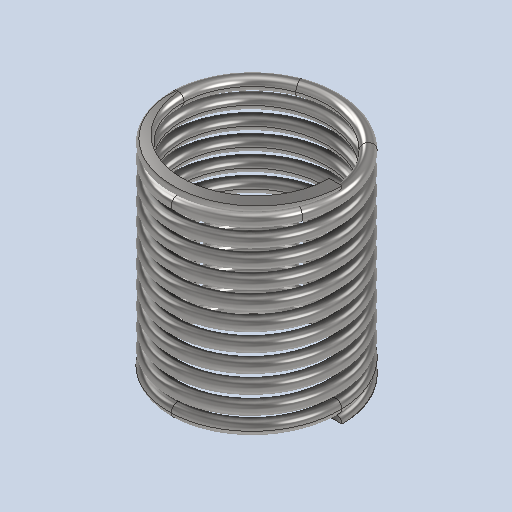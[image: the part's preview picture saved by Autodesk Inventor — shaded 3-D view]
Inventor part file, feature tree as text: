
AUTODESK INVENTOR PART (.ipt)
format: ipt  version: 2025 (Build 290162010, 162A)  size: 1,136,640 bytes
history: native  units: mm
features: other x65, extrude x8, plane x5, helix x3, sketch x3, sweep x2
ambient origin geometry x8: Origin, YZ Plane, XZ Plane, XY Plane, X Axis, Y Axis, Z Axis, Center Point
bodies: Solid1 (feature_tree)
feature tree (86):
  other  "Hauptschraubenpfad(Rechts)"
  other  "Profilarbeitsebene(Rechts)"
  plane  "Arbeitsebene(Rechts) starten"
  plane  "Arbeitsebene(Rechts) beenden"
  other  "Schnittarbeitsebene(Rechts) beenden"
  other  "Schnittarbeitsebene(Rechts) starten"
  other  "Schnittarbeitsebene mit flachen Enden 1(Rechts)"
  other  "Schnittarbeitsebene mit flachen Enden 2(Rechts)"
  sweep  "Main Coil Feature(R)"
  other  "Übergangsschraube 1(Rechts) starten"
  helix  "Coil  Start Transition 2(R)"  [1 undecoded]
  helix  "Coil  Start Transition 3(R)"  [1 undecoded]
  helix  "Coil  Start Transition 4(R)"  [1 undecoded]
  other  "Endenschraube(Rechts) starten"
  extrude  "Schnittelement(Rechts) starten"  Depth=10.0mm
  other  "Übergangsschraube 1(Rechts) beenden"
  other  "Übergangsschraube 2(Rechts) beenden"
  other  "Übergangsschraube 3(Rechts) beenden"
  other  "Übergangsschraube 4(Rechts) beenden"
  other  "Spirale(Rechts) beenden"
  extrude  "Schnittelement(Rechts) beenden"  Depth=10.0mm
  extrude  "Schnittelement mit flachen Enden 1(Rechts)"  Depth=10.0mm
  extrude  "Plain Ends Cut  2(R)"  Depth=10.0mm TaperAngle=0.0deg
  other  "Hauptschraubenpfad(Links)"
  other  "Profilarbeitsebene(Links)"
  plane  "Arbeitsebene(Links) starten"
  plane  "Arbeitsebene(Links) beenden"
  other  "Schnittarbeitsebene(Links) beenden"
  other  "Schnittarbeitsebene(Links) starten"
  other  "Schnittarbeitsebene mit flachen Enden 1(Links)"
  other  "Schnittarbeitsebene mit flachen Enden 2(Links)"
  sweep  "Main Coil Feature(L)"
  other  "Übergangsschraube 1(Links) starten"
  other  "Übergangsschraube 2(Links) starten"
  other  "Übergangsschraube 3(Links) starten"
  other  "Übergangsschraube 4(Links) starten"
  other  "Endenschraube(Links) starten"
  extrude  "Schnittelement(Links) starten"  Depth=10.0mm TaperAngle=0.0deg
  other  "Übergangsschraube 1(Links) beenden"
  other  "Übergangsschraube 2(Links) beenden"
  other  "Übergangsschraube 3(Links) beenden"
  other  "Übergangsschraube 4(Links) beenden"
  other  "Spirale(Links) beenden"
  extrude  "Schnittelement(Links) beenden"  Depth=10.0mm
  extrude  "Cut Plain Ends Cut 1(L)"  TaperAngle=0.0deg  [1 undecoded]
  extrude  "Cut Plain Ends Cut 2(L)"  TaperAngle=0.0deg  [1 undecoded]
  other  "iMate-basierte Arbeitsebene"
  other  "Vorschau Mittelpunkt"
  other  "Vorschau X-Achse"
  other  "Pfadprofilskizze(Rechts)"
  other  "Srf1"
  other  "Spiralenprofilskizze(Rechts)"
  other  "Übergangsschraubenskizze 1(Rechts) starten"
  sketch  "Sketch  Start Transition 2(R)"  dims[d0=0.125mm d2=0.701927mm d3=10.0mm d4=92.5mm]
  sketch  "Sketch  Start Transition 3(R)"  dims[d5=0.0mm d6=90.0deg d7=90.0deg d8=0.0mm d9=0.0mm d12=0.681625mm d13=-0.825556mm d14=0.5mm]
  sketch  "Sketch  Start Transition 4(R)"  dims[d15=0.0mm d16=0.651446mm d17=10.0mm d18=2.5mm d19=0.0mm d20=90.0deg d21=90.0deg d22=0.0mm d23=0.0mm d24=0.600964mm d25=10.0mm d26=2.5mm d27=0.0mm d28=90.0deg d29=90.0deg d30=0.0mm d31=0.0mm d32=0.550482mm d33=10.0mm d34=2.5mm d35=0.0mm d36=90.0deg d37=90.0deg d38=0.0mm d39=0.0mm d40=0.5mm d41=10.0mm d42=2.5mm d43=0.0mm d44=90.0deg d45=90.0deg d46=0.0mm d47=0.0mm d48=0.651446mm d49=10.0mm d50=1.875mm d51=0.0mm d52=90.0deg d53=90.0deg d54=0.0mm d55=0.0mm d56=0.600964mm d57=10.0mm d58=1.875mm d59=0.0mm d60=90.0deg d61=90.0deg d62=0.0mm d63=0.0mm d64=0.550482mm d65=10.0mm d66=1.875mm d67=0.0mm d68=90.0deg d69=90.0deg d70=0.0mm d71=0.0mm d72=0.5mm d73=10.0mm d74=1.875mm d75=0.0mm d76=90.0deg d77=90.0deg d78=0.0mm d79=0.0mm d81=10.0mm d82=5.0mm d83=0.0mm d84=90.0deg d85=90.0deg d86=0.0mm d87=0.0mm d88=0.500334mm d89=10.0mm d90=5.0mm d91=0.0mm d92=90.0deg d93=90.0deg d94=0.0mm d95=0.0mm d96=6.6153mm d97=0.500334mm d98=0.0mm d99=6.6153mm d100=0.500334mm d101=0.0mm d102=0.0mm d103=0.0mm d104=0.0mm d105=0.0mm d106=0.0mm d108=0.0mm d112=0.0mm d113=0.0mm d114=0.0mm d121=0.000334mm d131=0.0mm d132=0.0mm d133=0.0mm d134=0.0mm d135=0.125mm d137=0.701927mm d138=10.0mm d139=92.5mm d140=0.0mm d141=90.0deg d142=90.0deg d143=0.0mm d144=0.0mm d145=0.681625mm d146=-0.825556mm d147=0.000334mm d148=0.000334mm d149=0.5mm d150=0.0mm d151=0.0mm d152=0.651446mm d153=10.0mm d154=2.5mm d155=0.0mm d156=90.0deg d157=90.0deg d158=0.0mm d159=0.0mm d160=0.600964mm d161=10.0mm d162=2.5mm d163=0.0mm d164=90.0deg d165=90.0deg d166=0.0mm d167=0.0mm d168=0.550482mm d169=10.0mm d170=2.5mm d171=0.0mm d172=90.0deg d173=90.0deg d174=0.0mm d175=0.0mm d176=0.5mm d177=10.0mm d178=2.5mm d179=0.0mm d180=90.0deg d181=90.0deg d182=0.0mm d183=0.0mm d184=10.0mm d185=10.0mm d186=10.0mm d187=10.0mm d188=0.500334mm d189=10.0mm d190=5.0mm d191=0.0mm d192=90.0deg d193=90.0deg d194=0.0mm d195=0.0mm d196=10.0mm d197=6.6153mm d198=0.500334mm d199=0.0mm d200=10.0mm d201=0.651446mm d202=10.0mm d203=1.875mm d204=0.0mm d205=90.0deg d206=90.0deg d207=0.0mm d208=0.0mm d209=10.0mm d210=0.600964mm d211=10.0mm d212=1.875mm d213=0.0mm d214=90.0deg d215=90.0deg d216=0.0mm d217=0.0mm d218=0.550482mm d219=10.0mm d220=1.875mm d221=0.0mm d222=90.0deg d223=90.0deg d224=0.0mm d225=0.0mm d226=0.5mm d227=10.0mm d228=1.875mm d229=0.0mm d230=90.0deg d231=90.0deg d232=0.0mm d233=0.0mm d234=10.0mm d235=10.0mm d236=10.0mm d237=0.500334mm d238=10.0mm d239=5.0mm d240=0.0mm d241=90.0deg d242=90.0deg d243=0.0mm d244=0.0mm d245=6.6153mm d246=0.500334mm d247=0.0mm d248=10.0mm d249=10.0mm d254=6.6153mm d255=10.0mm d256=0.0mm d257=20.0mm d258=-0.000334mm d259=6.6153mm d260=10.0mm d261=0.0mm d262=10.0mm d263=6.6153mm d264=10.0mm d265=0.0mm d266=10.0mm d267=0.0mm d270=-0.763056mm d271=0.0mm d272=6.6153mm d273=10.0mm d274=0.0mm d275=20.0mm d276=-94.24778mm d277=6.1153mm d278=6.1153mm d279=0.0mm d280=0.0mm]
  other  "Übergangsschraubenskizze 1(Rechts) beenden"
  other  "Übergangsschraubenskizze 2(Rechts) beenden"
  other  "Übergangsschraubenskizze 3(Rechts) beenden"
  other  "Übergangsschraubenskizze 4(Rechts) beenden"
  other  "Endenskizze(Rechts) starten"
  other  "Spiralenskizze(Rechts) beenden"
  other  "Schnittskizze(Rechts) beenden"
  other  "Schnittskizze (Rechts) starten"
  other  "Pfadprofilskizze(Links)"
  other  "Srf2"
  other  "Spiralenprofilskizze(Links)"
  other  "Übergangsschraubenskizze 1(Links) starten"
  other  "Übergangsschraubenskizze 2(Links) starten"
  other  "Übergangsschraubenskizze 3(Links) starten"
  other  "Übergangsschraubenskizze 4(Links) starten"
  other  "Endenskizze(Links) starten"
  other  "Schnittskizze(Links) starten"
  other  "Übergangsschraubenskizze 1(Links) beenden"
  other  "Übergangsschraubenskizze 2(Links) beenden"
  other  "Übergangsschraubenskizze 3(Links) beenden"
  other  "Übergangsschraubenskizze 4(Links) beenden"
  other  "Spiralenskizze(Links) beenden"
  other  "Schnittskizze(Links) beenden"
  other  "Schnittskizze mit flachen Enden 2(Links)"
  other  "Schnittskizze mit flachen Enden 2(Rechts)"
  other  "Schnittskizze mit flachen Enden 1(Rechts)"
  other  "Schnittskizze mit flachen Enden 1(Links)"
  plane  "Arbeitsebene - Schnitt starten"
  other  "Basiskurve(Rechts)"
  other  "Basiskurve(Links)"
note: 5 required parameter values undecoded (feature->parameter linkage not recoverable at this tier; creation-order binding heuristic only, values carry confidence <= 0.55)
